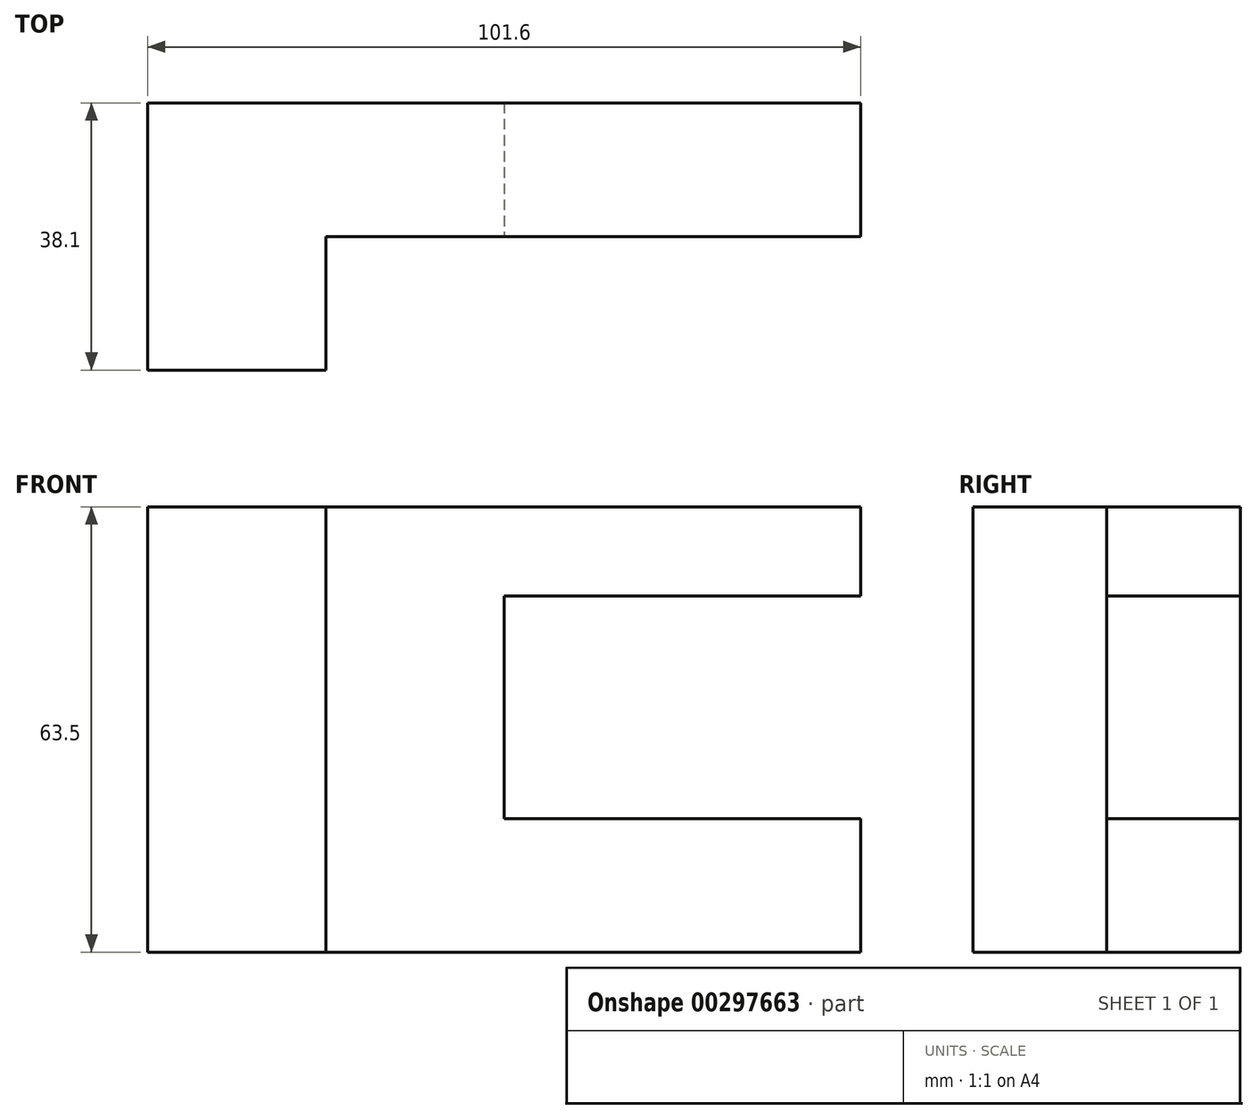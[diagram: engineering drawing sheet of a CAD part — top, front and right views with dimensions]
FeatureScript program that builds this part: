
annotation { "Feature Type Name" : "Feature", "Feature Type Description" : "" }
export const myFeature = defineFeature(function(context is Context, id is Id, definition is map)
    precondition{}
    {
        {
            var Q0;
            Q0=qCreatedBy(makeId("Front.planeOp"),FACE);
            var sketch = newSketch(context, id + "F0", { "sketchPlane" : qUnion([Q0])});
            skLineSegment(sketch, "E0.bottom", {"start": v(50.8, 31.75) * mm, "end": v(-50.8, 31.75) * mm});
            skLineSegment(sketch, "E0.top", {"start": v(50.8, -31.75) * mm, "end": v(-50.8, -31.75) * mm});
            skLineSegment(sketch, "E0.left", {"start": v(50.8, 31.75) * mm, "end": v(50.8, -31.75) * mm});
            skLineSegment(sketch, "E0.right", {"start": v(-50.8, 31.75) * mm, "end": v(-50.8, -31.75) * mm});
            skPoint(sketch, "E0.middle", {"position": v(0, 0) * mm});
            skSolve(sketch);
        }
        {
            var Q0;
            Q0=makeQuery(id+"F0.imprint","IMPRINT",FACE,{"disambiguationData":[TD([[makeQuery(id+"F0.imprint","IMPRINT",EDGE,{"derivedFrom":sQuery(id+"F0.wireOp",EDGE,"E0.bottom")}),1.0]])]});
            extrude(context, id + "F1", {"entities" : qUnion([Q0]), "depth" : 19.05 * mm});
        }
        {
            var Q0;
            Q0=makeQuery(id+"F1.opExtrude","CAP_FACE",FACE,{"disambiguationData":[OSD([sQuery(id+"F0.wireOp",EDGE,"E0.bottom"),sQuery(id+"F0.wireOp",EDGE,"E0.top"),sQuery(id+"F0.wireOp",EDGE,"E0.left"),sQuery(id+"F0.wireOp",EDGE,"E0.right")])],"isStart":false});
            var sketch = newSketch(context, id + "F2", { "sketchPlane" : qUnion([Q0])});
            skLineSegment(sketch, "E1.bottom", {"start": v(50.8, 19.05) * mm, "end": v(0, 19.05) * mm});
            skLineSegment(sketch, "E1.top", {"start": v(50.8, -12.7) * mm, "end": v(0, -12.7) * mm});
            skLineSegment(sketch, "E1.left", {"start": v(50.8, 19.05) * mm, "end": v(50.8, -12.7) * mm});
            skLineSegment(sketch, "E1.right", {"start": v(0, 19.05) * mm, "end": v(0, -12.7) * mm});
            skSolve(sketch);
        }
        {
            var Q0;
            Q0=makeQuery(id+"F2.imprint","IMPRINT",FACE,{"disambiguationData":[TD([[makeQuery(id+"F2.imprint","IMPRINT",EDGE,{"derivedFrom":sQuery(id+"F2.wireOp",EDGE,"E1.bottom")}),1.0]])]});
            extrude(context, id + "F3", {"entities" : qUnion([Q0]), "operationType" : NewBodyOperationType.REMOVE, "endBound" : BoundingType.THROUGH_ALL, "oppositeDirection" : true, "depth" : 25.4 * mm});
        }
        {
            var Q0;
            Q0=makeQuery(id+"F1.opExtrude","CAP_FACE",FACE,{"disambiguationData":[OSD([sQuery(id+"F0.wireOp",EDGE,"E0.bottom"),sQuery(id+"F0.wireOp",EDGE,"E0.top"),sQuery(id+"F0.wireOp",EDGE,"E0.left"),sQuery(id+"F0.wireOp",EDGE,"E0.right")])],"isStart":false});
            var sketch = newSketch(context, id + "F4", { "sketchPlane" : qUnion([Q0])});
            skLineSegment(sketch, "E2.bottom", {"start": v(-25.4, 31.75) * mm, "end": v(-50.8, 31.75) * mm});
            skLineSegment(sketch, "E2.top", {"start": v(-25.4, -31.75) * mm, "end": v(-50.8, -31.75) * mm});
            skLineSegment(sketch, "E2.left", {"start": v(-25.4, 31.75) * mm, "end": v(-25.4, -31.75) * mm});
            skLineSegment(sketch, "E2.right", {"start": v(-50.8, 31.75) * mm, "end": v(-50.8, -31.75) * mm});
            skSolve(sketch);
        }
        {
            var Q0;
            Q0 = qSketchRegion(id + "F4", true);
            extrude(context, id + "F5", {"entities" : qUnion([Q0]), "operationType" : NewBodyOperationType.ADD, "depth" : 19.05 * mm});
        }
    });
